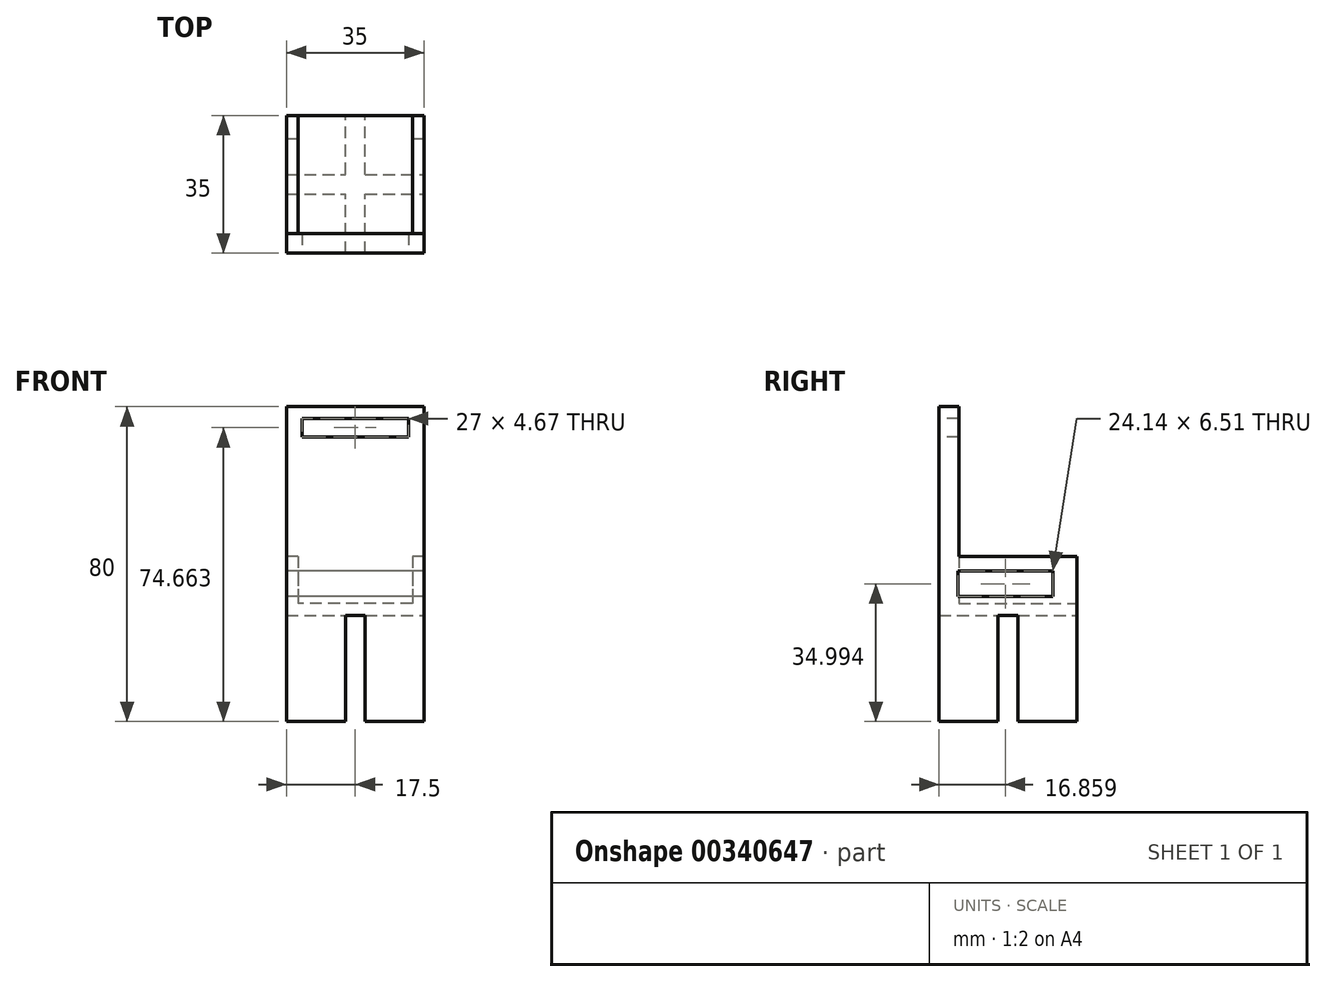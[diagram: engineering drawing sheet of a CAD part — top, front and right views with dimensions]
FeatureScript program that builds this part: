
annotation { "Feature Type Name" : "Feature", "Feature Type Description" : "" }
export const myFeature = defineFeature(function(context is Context, id is Id, definition is map)
    precondition{}
    {
        {
            var Q0;
            Q0=qCreatedBy(makeId("Top.planeOp"),FACE);
            var sketch = newSketch(context, id + "F0", { "sketchPlane" : qUnion([Q0])});
            skLineSegment(sketch, "E0.bottom", {"start": v(0, 0) * mm, "end": v(15, 0) * mm});
            skLineSegment(sketch, "E0.top", {"start": v(0, 15) * mm, "end": v(15, 15) * mm});
            skLineSegment(sketch, "E0.left", {"start": v(0, 0) * mm, "end": v(0, 15) * mm});
            skLineSegment(sketch, "E0.right", {"start": v(15, 0) * mm, "end": v(15, 15) * mm});
            skLineSegment(sketch, "E1.0.1.0", {"start": v(0, 35) * mm, "end": v(15, 35) * mm});
            skLineSegment(sketch, "E1.0.1.1", {"start": v(0, 20) * mm, "end": v(0, 35) * mm});
            skLineSegment(sketch, "E1.0.1.2", {"start": v(0, 20) * mm, "end": v(15, 20) * mm});
            skLineSegment(sketch, "E1.0.1.3", {"start": v(15, 20) * mm, "end": v(15, 35) * mm});
            skLineSegment(sketch, "E1.1.0.0", {"start": v(20, 15) * mm, "end": v(35, 15) * mm});
            skLineSegment(sketch, "E1.1.0.1", {"start": v(20, 0) * mm, "end": v(20, 15) * mm});
            skLineSegment(sketch, "E1.1.0.2", {"start": v(20, 0) * mm, "end": v(35, 0) * mm});
            skLineSegment(sketch, "E1.1.0.3", {"start": v(35, 0) * mm, "end": v(35, 15) * mm});
            skLineSegment(sketch, "E1.1.1.0", {"start": v(20, 35) * mm, "end": v(35, 35) * mm});
            skLineSegment(sketch, "E1.1.1.1", {"start": v(20, 20) * mm, "end": v(20, 35) * mm});
            skLineSegment(sketch, "E1.1.1.2", {"start": v(20, 20) * mm, "end": v(35, 20) * mm});
            skLineSegment(sketch, "E1.1.1.3", {"start": v(35, 20) * mm, "end": v(35, 35) * mm});
            skLineSegment(sketch, "E1.direction1", {"start": v(0, 15) * mm, "end": v(20, 15) * mm, "construction": true});
            skLineSegment(sketch, "E1.direction2", {"start": v(0, 15) * mm, "end": v(0, 35) * mm, "construction": true});
            skSolve(sketch);
        }
        {
            var Q0;
            Q0=makeQuery(id+"F0.imprint","IMPRINT",FACE,{"disambiguationData":[TD([[makeQuery(id+"F0.imprint","IMPRINT",EDGE,{"derivedFrom":sQuery(id+"F0.wireOp",EDGE,"E0.bottom")}),1.0]])]});
            var Q1;
            Q1=makeQuery(id+"F0.imprint","IMPRINT",FACE,{"disambiguationData":[TD([[makeQuery(id+"F0.imprint","IMPRINT",EDGE,{"derivedFrom":sQuery(id+"F0.wireOp",EDGE,"E1.0.1.0")}),-1.0]])]});
            var Q2;
            Q2=makeQuery(id+"F0.imprint","IMPRINT",FACE,{"disambiguationData":[TD([[makeQuery(id+"F0.imprint","IMPRINT",EDGE,{"derivedFrom":sQuery(id+"F0.wireOp",EDGE,"E1.1.1.0")}),-1.0]])]});
            var Q3;
            Q3=makeQuery(id+"F0.imprint","IMPRINT",FACE,{"disambiguationData":[TD([[makeQuery(id+"F0.imprint","IMPRINT",EDGE,{"derivedFrom":sQuery(id+"F0.wireOp",EDGE,"E1.1.0.0")}),-1.0]])]});
            extrude(context, id + "F1", {"entities" : qUnion([Q0, Q1, Q2, Q3]), "depth" : 30 * mm});
        }
        {
            var Q0;
            Q0=makeQuery(id+"F1.opExtrude","CAP_FACE",FACE,{"disambiguationData":[OSD([sQuery(id+"F0.wireOp",EDGE,"E1.0.1.0"),sQuery(id+"F0.wireOp",EDGE,"E1.0.1.1"),sQuery(id+"F0.wireOp",EDGE,"E1.0.1.2"),sQuery(id+"F0.wireOp",EDGE,"E1.0.1.3")])],"isStart":false});
            var sketch = newSketch(context, id + "F2", { "sketchPlane" : qUnion([Q0])});
            skSolve(sketch);
        }
        {
            var Q0;
            Q0=makeQuery(id+"F2.imprint","IMPRINT",FACE,{"disambiguationData":[TD([[makeQuery(id+"F2.imprint","IMPRINT",EDGE,{"derivedFrom":makeQuery(id+"F1.opExtrude","CAP_EDGE",EDGE,{"disambiguationData":[OSD([sQuery(id+"F0.wireOp",EDGE,"E1.0.1.0")])],"isStart":false})}),-1.0]])]});
            var sketch = newSketch(context, id + "F3", { "sketchPlane" : qUnion([Q0])});
            skLineSegment(sketch, "E2.bottom", {"start": v(0, 35) * mm, "end": v(35, 35) * mm});
            skLineSegment(sketch, "E2.top", {"start": v(0, 0) * mm, "end": v(35, 0) * mm});
            skLineSegment(sketch, "E2.left", {"start": v(0, 35) * mm, "end": v(0, 0) * mm});
            skLineSegment(sketch, "E2.right", {"start": v(35, 35) * mm, "end": v(35, 0) * mm});
            skSolve(sketch);
        }
        {
            var Q0;
            Q0 = qSketchRegion(id + "F3", true);
            extrude(context, id + "F4", {"entities" : qUnion([Q0]), "operationType" : NewBodyOperationType.ADD, "oppositeDirection" : true, "depth" : 3 * mm});
        }
        {
            var Q0;
            Q0=makeQuery(id+"F4.boolean.opBoolean","MERGE",FACE,{"derivedFrom":[makeQuery(id+"F1.opExtrude","CAP_FACE",FACE,{"disambiguationData":[OSD([sQuery(id+"F0.wireOp",EDGE,"E0.bottom"),sQuery(id+"F0.wireOp",EDGE,"E0.top"),sQuery(id+"F0.wireOp",EDGE,"E0.left"),sQuery(id+"F0.wireOp",EDGE,"E0.right")])],"isStart":false}),makeQuery(id+"F1.opExtrude","CAP_FACE",FACE,{"disambiguationData":[OSD([sQuery(id+"F0.wireOp",EDGE,"E1.0.1.0"),sQuery(id+"F0.wireOp",EDGE,"E1.0.1.1"),sQuery(id+"F0.wireOp",EDGE,"E1.0.1.2"),sQuery(id+"F0.wireOp",EDGE,"E1.0.1.3")])],"isStart":false}),makeQuery(id+"F1.opExtrude","CAP_FACE",FACE,{"disambiguationData":[OSD([sQuery(id+"F0.wireOp",EDGE,"E1.1.0.0"),sQuery(id+"F0.wireOp",EDGE,"E1.1.0.1"),sQuery(id+"F0.wireOp",EDGE,"E1.1.0.2"),sQuery(id+"F0.wireOp",EDGE,"E1.1.0.3")])],"isStart":false}),makeQuery(id+"F1.opExtrude","CAP_FACE",FACE,{"disambiguationData":[OSD([sQuery(id+"F0.wireOp",EDGE,"E1.1.1.0"),sQuery(id+"F0.wireOp",EDGE,"E1.1.1.1"),sQuery(id+"F0.wireOp",EDGE,"E1.1.1.2"),sQuery(id+"F0.wireOp",EDGE,"E1.1.1.3")])],"isStart":false}),makeQuery(id+"F4.opExtrude","CAP_FACE",FACE,{"disambiguationData":[OSD([sQuery(id+"F3.wireOp",EDGE,"E2.bottom"),sQuery(id+"F3.wireOp",EDGE,"E2.top"),sQuery(id+"F3.wireOp",EDGE,"E2.left"),sQuery(id+"F3.wireOp",EDGE,"E2.right")])],"isStart":true})]});
            var sketch = newSketch(context, id + "F5", { "sketchPlane" : qUnion([Q0])});
            skLineSegment(sketch, "E3.bottom", {"start": v(35, 0) * mm, "end": v(0, 0) * mm});
            skLineSegment(sketch, "E3.top", {"start": v(35, 5) * mm, "end": v(0, 5) * mm});
            skLineSegment(sketch, "E3.left", {"start": v(35, 0) * mm, "end": v(35, 5) * mm});
            skLineSegment(sketch, "E3.right", {"start": v(0, 0) * mm, "end": v(0, 5) * mm});
            skSolve(sketch);
        }
        {
            var Q0;
            Q0=makeQuery(id+"F5.imprint","IMPRINT",FACE,{"disambiguationData":[TD([[makeQuery(id+"F5.imprint","IMPRINT",EDGE,{"derivedFrom":sQuery(id+"F5.wireOp",EDGE,"E3.bottom")}),1.0]])]});
            extrude(context, id + "F6", {"entities" : qUnion([Q0]), "operationType" : NewBodyOperationType.ADD, "depth" : 50 * mm});
        }
        {
            var Q0;
            Q0=makeQuery(id+"F6.boolean.opBoolean","MERGE",FACE,{"derivedFrom":[makeQuery(id+"F4.boolean.opBoolean","MERGE",FACE,{"derivedFrom":[makeQuery(id+"F1.opExtrude","SWEPT_FACE",FACE,{"disambiguationData":[OSD([sQuery(id+"F0.wireOp",EDGE,"E0.bottom")])]}),makeQuery(id+"F1.opExtrude","SWEPT_FACE",FACE,{"disambiguationData":[OSD([sQuery(id+"F0.wireOp",EDGE,"E1.1.0.2")])]}),makeQuery(id+"F4.opExtrude","SWEPT_FACE",FACE,{"disambiguationData":[OSD([sQuery(id+"F3.wireOp",EDGE,"E2.top")])]})]}),makeQuery(id+"F6.opExtrude","SWEPT_FACE",FACE,{"disambiguationData":[OSD([sQuery(id+"F5.wireOp",EDGE,"E3.bottom")])]})]});
            var sketch = newSketch(context, id + "F7", { "sketchPlane" : qUnion([Q0])});
            skLineSegment(sketch, "E4.bottom", {"start": v(31, 77) * mm, "end": v(4, 77) * mm});
            skLineSegment(sketch, "E4.top", {"start": v(31, 72.33) * mm, "end": v(4, 72.33) * mm});
            skLineSegment(sketch, "E4.left", {"start": v(31, 77) * mm, "end": v(31, 72.33) * mm});
            skLineSegment(sketch, "E4.right", {"start": v(4, 77) * mm, "end": v(4, 72.33) * mm});
            skSolve(sketch);
        }
        {
            var Q0;
            Q0=makeQuery(id+"F7.imprint","IMPRINT",FACE,{"disambiguationData":[TD([[makeQuery(id+"F7.imprint","IMPRINT",EDGE,{"derivedFrom":sQuery(id+"F7.wireOp",EDGE,"E4.bottom")}),1.0]])]});
            extrude(context, id + "F8", {"entities" : qUnion([Q0]), "operationType" : NewBodyOperationType.REMOVE, "oppositeDirection" : true, "depth" : 25 * mm});
        }
        {
            var Q0;
            Q0=makeQuery(id+"F4.boolean.opBoolean","MERGE",FACE,{"derivedFrom":[makeQuery(id+"F1.opExtrude","CAP_FACE",FACE,{"disambiguationData":[OSD([sQuery(id+"F0.wireOp",EDGE,"E0.bottom"),sQuery(id+"F0.wireOp",EDGE,"E0.top"),sQuery(id+"F0.wireOp",EDGE,"E0.left"),sQuery(id+"F0.wireOp",EDGE,"E0.right")])],"isStart":false}),makeQuery(id+"F1.opExtrude","CAP_FACE",FACE,{"disambiguationData":[OSD([sQuery(id+"F0.wireOp",EDGE,"E1.0.1.0"),sQuery(id+"F0.wireOp",EDGE,"E1.0.1.1"),sQuery(id+"F0.wireOp",EDGE,"E1.0.1.2"),sQuery(id+"F0.wireOp",EDGE,"E1.0.1.3")])],"isStart":false}),makeQuery(id+"F1.opExtrude","CAP_FACE",FACE,{"disambiguationData":[OSD([sQuery(id+"F0.wireOp",EDGE,"E1.1.0.0"),sQuery(id+"F0.wireOp",EDGE,"E1.1.0.1"),sQuery(id+"F0.wireOp",EDGE,"E1.1.0.2"),sQuery(id+"F0.wireOp",EDGE,"E1.1.0.3")])],"isStart":false}),makeQuery(id+"F1.opExtrude","CAP_FACE",FACE,{"disambiguationData":[OSD([sQuery(id+"F0.wireOp",EDGE,"E1.1.1.0"),sQuery(id+"F0.wireOp",EDGE,"E1.1.1.1"),sQuery(id+"F0.wireOp",EDGE,"E1.1.1.2"),sQuery(id+"F0.wireOp",EDGE,"E1.1.1.3")])],"isStart":false}),makeQuery(id+"F4.opExtrude","CAP_FACE",FACE,{"disambiguationData":[OSD([sQuery(id+"F3.wireOp",EDGE,"E2.bottom"),sQuery(id+"F3.wireOp",EDGE,"E2.top"),sQuery(id+"F3.wireOp",EDGE,"E2.left"),sQuery(id+"F3.wireOp",EDGE,"E2.right")])],"isStart":true})]});
            var sketch = newSketch(context, id + "F9", { "sketchPlane" : qUnion([Q0])});
            skLineSegment(sketch, "E5.bottom", {"start": v(35, 5) * mm, "end": v(32, 5) * mm});
            skLineSegment(sketch, "E5.top", {"start": v(35, 35) * mm, "end": v(32, 35) * mm});
            skLineSegment(sketch, "E5.left", {"start": v(35, 5) * mm, "end": v(35, 35) * mm});
            skLineSegment(sketch, "E5.right", {"start": v(32, 5) * mm, "end": v(32, 35) * mm});
            skLineSegment(sketch, "E6.bottom", {"start": v(0, 5) * mm, "end": v(3, 5) * mm});
            skLineSegment(sketch, "E6.top", {"start": v(0, 35) * mm, "end": v(3, 35) * mm});
            skLineSegment(sketch, "E6.left", {"start": v(0, 5) * mm, "end": v(0, 35) * mm});
            skLineSegment(sketch, "E6.right", {"start": v(3, 5) * mm, "end": v(3, 35) * mm});
            skSolve(sketch);
        }
        {
            var Q0;
            Q0 = qSketchRegion(id + "F9", true);
            extrude(context, id + "F10", {"entities" : qUnion([Q0]), "operationType" : NewBodyOperationType.ADD, "depth" : 12 * mm});
        }
        {
            var Q0;
            Q0=makeQuery(id+"F10.boolean.opBoolean","MERGE",FACE,{"derivedFrom":[makeQuery(id+"F6.boolean.opBoolean","MERGE",FACE,{"derivedFrom":[makeQuery(id+"F4.boolean.opBoolean","MERGE",FACE,{"derivedFrom":[makeQuery(id+"F1.opExtrude","SWEPT_FACE",FACE,{"disambiguationData":[OSD([sQuery(id+"F0.wireOp",EDGE,"E1.1.0.3")])]}),makeQuery(id+"F1.opExtrude","SWEPT_FACE",FACE,{"disambiguationData":[OSD([sQuery(id+"F0.wireOp",EDGE,"E1.1.1.3")])]}),makeQuery(id+"F4.opExtrude","SWEPT_FACE",FACE,{"disambiguationData":[OSD([sQuery(id+"F3.wireOp",EDGE,"E2.right")])]})]}),makeQuery(id+"F6.opExtrude","SWEPT_FACE",FACE,{"disambiguationData":[OSD([sQuery(id+"F5.wireOp",EDGE,"E3.left")])]})]}),makeQuery(id+"F10.opExtrude","SWEPT_FACE",FACE,{"disambiguationData":[OSD([sQuery(id+"F9.wireOp",EDGE,"E5.left")])]})]});
            var sketch = newSketch(context, id + "F11", { "sketchPlane" : qUnion([Q0])});
            skLineSegment(sketch, "E7.bottom", {"start": v(7.64, 37.08) * mm, "end": v(31.45, 37.08) * mm});
            skLineSegment(sketch, "E7.top", {"start": v(7.64, 32.71) * mm, "end": v(31.45, 32.71) * mm});
            skLineSegment(sketch, "E7.left", {"start": v(7.64, 37.08) * mm, "end": v(7.64, 32.71) * mm});
            skLineSegment(sketch, "E7.right", {"start": v(31.45, 37.08) * mm, "end": v(31.45, 32.71) * mm});
            skSolve(sketch);
        }
        {
            var Q0;
            Q0=makeQuery(id+"F10.boolean.opBoolean","MERGE",FACE,{"derivedFrom":[makeQuery(id+"F6.boolean.opBoolean","MERGE",FACE,{"derivedFrom":[makeQuery(id+"F4.boolean.opBoolean","MERGE",FACE,{"derivedFrom":[makeQuery(id+"F1.opExtrude","SWEPT_FACE",FACE,{"disambiguationData":[OSD([sQuery(id+"F0.wireOp",EDGE,"E0.left")])]}),makeQuery(id+"F1.opExtrude","SWEPT_FACE",FACE,{"disambiguationData":[OSD([sQuery(id+"F0.wireOp",EDGE,"E1.0.1.1")])]}),makeQuery(id+"F4.opExtrude","SWEPT_FACE",FACE,{"disambiguationData":[OSD([sQuery(id+"F3.wireOp",EDGE,"E2.left")])]})]}),makeQuery(id+"F6.opExtrude","SWEPT_FACE",FACE,{"disambiguationData":[OSD([sQuery(id+"F5.wireOp",EDGE,"E3.right")])]})]}),makeQuery(id+"F10.opExtrude","SWEPT_FACE",FACE,{"disambiguationData":[OSD([sQuery(id+"F9.wireOp",EDGE,"E6.left")])]})]});
            var sketch = newSketch(context, id + "F12", { "sketchPlane" : qUnion([Q0])});
            skLineSegment(sketch, "E8.bottom", {"start": v(-4.79, 38.25) * mm, "end": v(-28.93, 38.25) * mm});
            skLineSegment(sketch, "E8.top", {"start": v(-4.79, 31.74) * mm, "end": v(-28.93, 31.74) * mm});
            skLineSegment(sketch, "E8.left", {"start": v(-4.79, 38.25) * mm, "end": v(-4.79, 31.74) * mm});
            skLineSegment(sketch, "E8.right", {"start": v(-28.93, 38.25) * mm, "end": v(-28.93, 31.74) * mm});
            skSolve(sketch);
        }
        {
            var Q0;
            Q0=makeQuery(id+"F12.imprint","IMPRINT",FACE,{"disambiguationData":[TD([[makeQuery(id+"F12.imprint","IMPRINT",EDGE,{"derivedFrom":sQuery(id+"F12.wireOp",EDGE,"E8.bottom")}),1.0]])]});
            var Q1;
            Q1=makeQuery(id+"F11.imprint","IMPRINT",FACE,{"disambiguationData":[TD([[makeQuery(id+"F11.imprint","IMPRINT",EDGE,{"derivedFrom":sQuery(id+"F11.wireOp",EDGE,"E7.bottom")}),-1.0]])]});
            extrude(context, id + "F13", {"entities" : qUnion([Q0, Q1]), "operationType" : NewBodyOperationType.REMOVE, "oppositeDirection" : true, "depth" : 349 * mm});
        }
    });
